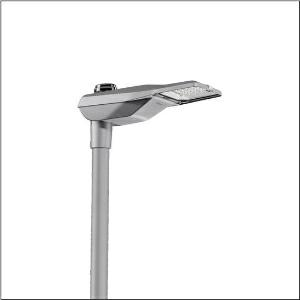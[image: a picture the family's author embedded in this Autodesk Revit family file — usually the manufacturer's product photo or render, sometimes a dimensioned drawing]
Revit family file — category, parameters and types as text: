
# Revit family: streetlight_sl_21_micro___st1_0a_5xe5d47n08cb_a602
name_source: partatom
category: Lighting Fixtures
units: mm (PartAtom-declared; Revit-internal decimal feet)

## family parameters
Cut with Voids When Loaded = No
Host = Face
Light Source = No
Part Type = Normal
Room Calculation Point = No
Round Connector Dimension = Use Diameter
Shared = No

## types (1)
- --- (1 x LED, 2380 lm, 15.8 W, 4000K)
    Apparent Load = 16 VA
    CIE Flux Codes = 37 72 97 100 100
    Color Rendering = 70
    Color Temperature = 4000K
    Default Elevation = 1800 mm
    Description = Streetlight SL 21 micro, mast luminaire, primary light control with lens, of PMMA, primary optical cover: cover, of toughened safety glass, transparent, light distribution: ST1.0a, light emission: direct distribution, primary light characteristic: asymmetric, installation type: post-top, LED, 3G 1.5mm², High Power LED, rated luminous flux: 2.380lm, luminous efficacy: 151lm/W, light colour: 740, colour temperature: 4000K, control: overheat protection, presetting dimming linear, constant luminous flux control, time-dependent luminous flux control, flexible luminous flux parameterisation, mains connection: 230..240V, AC, 50/60Hz, connection cable pre-assembled, cable length: 6,5m, wiring characteristics: H07RN-F, start of lifetime: 16W, end of service life: 16W, reduction: 8W, luminaire housing, of diecast aluminium (EN AC-44300), powder-coated, Siteco® metallic grey (DB 702S), corrosivity category C5 mid according to DIN EN ISO 12944, multi-level sealing system, sealing non-destructively replaceable, inclination adjustable: 0°, 5°, 10°, 15°, length: 528mm, width: 235mm, height: 110mm, spigot size: 76/60mm (post-top), protection rating (complete): IP66, insulation class (complete): insulation class I (protective earthing), certification: CE, ENEC, ENEC+, VDE, impact resistance: IK09, permissible operating ambient temperature for outdoor applications: -40..+50°C, standard-compliant lighting for roads and squares, packaging unit: 1 piece

Light Distribution: ST1.0a
    Height = 110 mm
    Lamp = 1 x LED
    Lamp Light Flux = 2380 lm
    Lamp Power = 15.8 W
    Lamp count = 1
    Length = 528 mm
    Luminous efficacy = 151 lm/W
    Manufacturer = Siteco
    ModVariant = No
    Model = 5XE5D47N08CB
    Number of Poles = 1
    OnlyDefault = Yes
    Power Factor = 1
    Product Name = Streetlight SL 21 micro | ST1.0a
    Product group = mast luminaire | pylon top
    ProductGroupID = 6100
    Protection Class = Protection class I
    Protection Degree = IP 66
    RLX_Detail_Level = 1
    RLX_Emergency_Light_Flux = 0 lm
    RLX_Emergency_Type = 0
    RLX_Emergency_Type_DB = No
    RlxData = <blob elided: 98565 chars, md5=fdc25e53>
    Socket = socket
    Standby Power = 0 W
    System Light Flux = 2380 lm
    System Power = 16 W
    Type Comments = factory setting: luminous flux: 100 % | dim-lin: 254 | 300 mA
    Type Image = l_1294375.jpg
    URL = http://relux.com
    VarID = @adj_085891
    Voltage = 0 V
    Weight = 0.00 kg
    Width = 235 mm

## geometry (parser evidence)
native form markers: Blend x4, Sweep x10
no freeform markers — native parametric forms only
